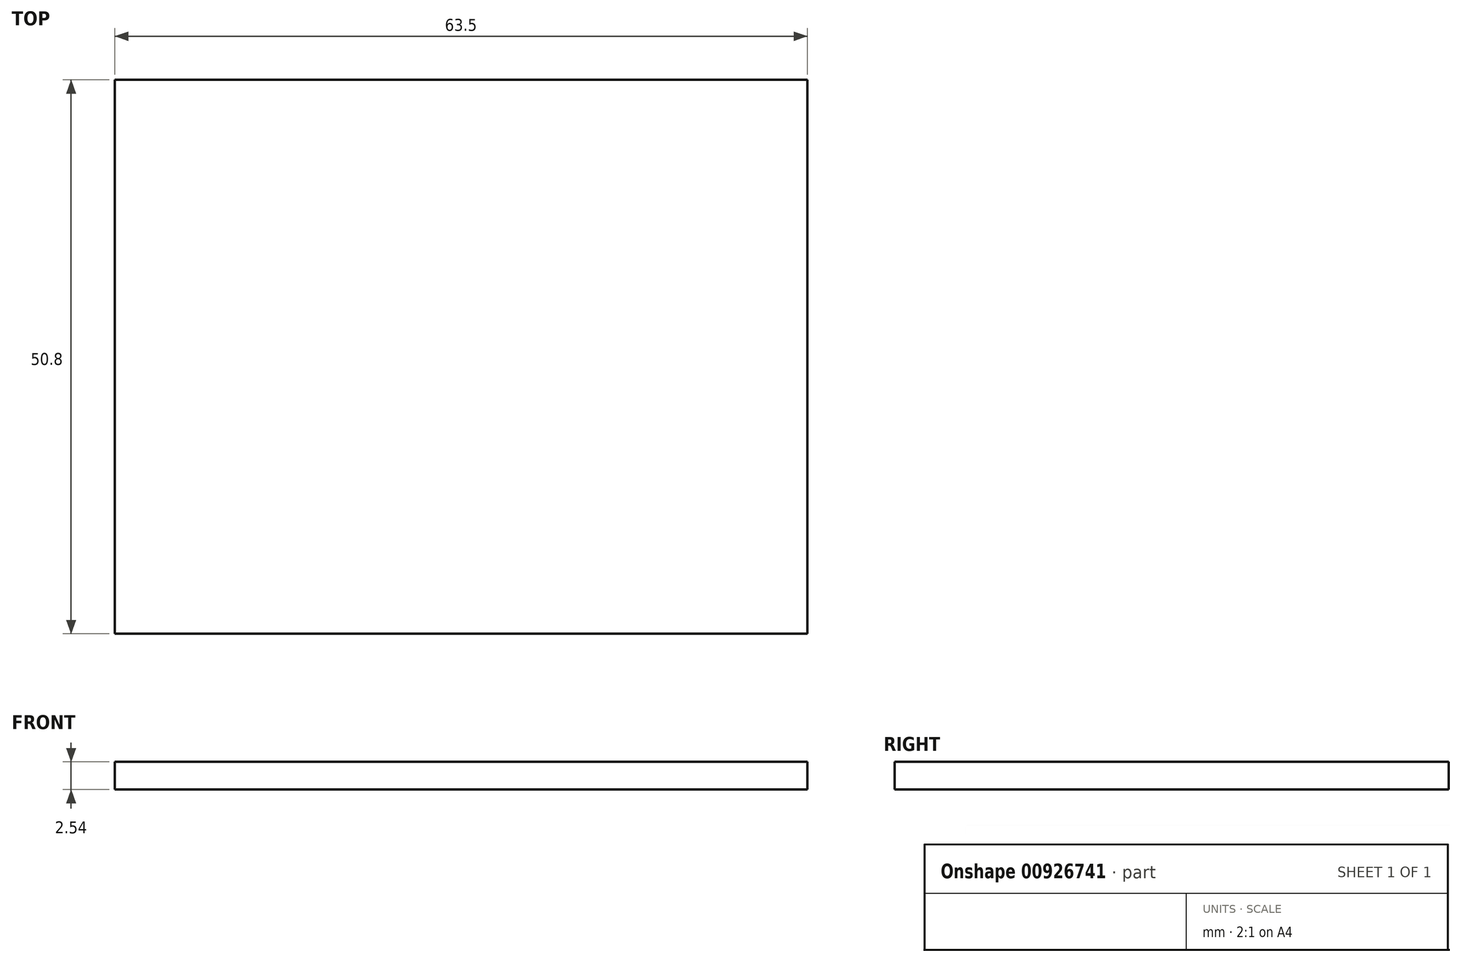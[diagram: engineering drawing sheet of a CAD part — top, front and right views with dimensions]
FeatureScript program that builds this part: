
annotation { "Feature Type Name" : "Feature", "Feature Type Description" : "" }
export const myFeature = defineFeature(function(context is Context, id is Id, definition is map)
    precondition{}
    {
        {
            var Q0;
            Q0=qCreatedBy(makeId("Top.planeOp"),FACE);
            var sketch = newSketch(context, id + "F0", { "sketchPlane" : qUnion([Q0])});
            skLineSegment(sketch, "E0.bottom", {"start": v(31.75, 25.4) * mm, "end": v(-31.75, 25.4) * mm});
            skLineSegment(sketch, "E0.top", {"start": v(31.75, -25.4) * mm, "end": v(-31.75, -25.4) * mm});
            skLineSegment(sketch, "E0.left", {"start": v(31.75, 25.4) * mm, "end": v(31.75, -25.4) * mm});
            skLineSegment(sketch, "E0.right", {"start": v(-31.75, 25.4) * mm, "end": v(-31.75, -25.4) * mm});
            skPoint(sketch, "E0.middle", {"position": v(0, 0) * mm});
            skSolve(sketch);
        }
        {
            var Q0;
            Q0=makeQuery(id+"F0.imprint","IMPRINT",FACE,{"disambiguationData":[TD([[makeQuery(id+"F0.imprint","IMPRINT",EDGE,{"derivedFrom":sQuery(id+"F0.wireOp",EDGE,"E0.bottom")}),1.0]])]});
            extrude(context, id + "F1", {"entities" : qUnion([Q0]), "endBound" : BoundingType.SYMMETRIC, "depth" : 2.54 * mm, "offsetDistance" : 25.4 * mm});
        }
    });
